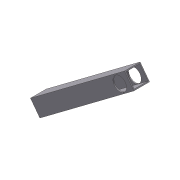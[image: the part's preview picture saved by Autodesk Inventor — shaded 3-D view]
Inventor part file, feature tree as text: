
AUTODESK INVENTOR PART (.ipt)
format: ipt  version: 2012 (Build 160160000, 160)  size: 87,552 bytes
history: native  units: in
note: dims shown in document units (in); Inventor stores cm internally (conversion verified against a paired STEP export)
features: extrude x2, sketch x2, shell x1
ambient origin geometry x8: Origin, YZ Plane, XZ Plane, XY Plane, X Axis, Y Axis, Z Axis, Center Point
bodies: Solid1 (feature_tree)
feature tree (5):
  extrude  "Extrusion1"  Depth=7.5in
  shell  "Shell1"  Thickness=1.0in
  extrude  "Extrusion2"  Depth=0.875in
  sketch  "Sketch1"  dims[d0=1.0in d1=7.5in d2=1.0in d3=0.0in]
  sketch  "Sketch2"  dims[d4=0.0625in d5=0.875in d6=0.5in d7=0.75in d8=1.0in d9=0.0in]
